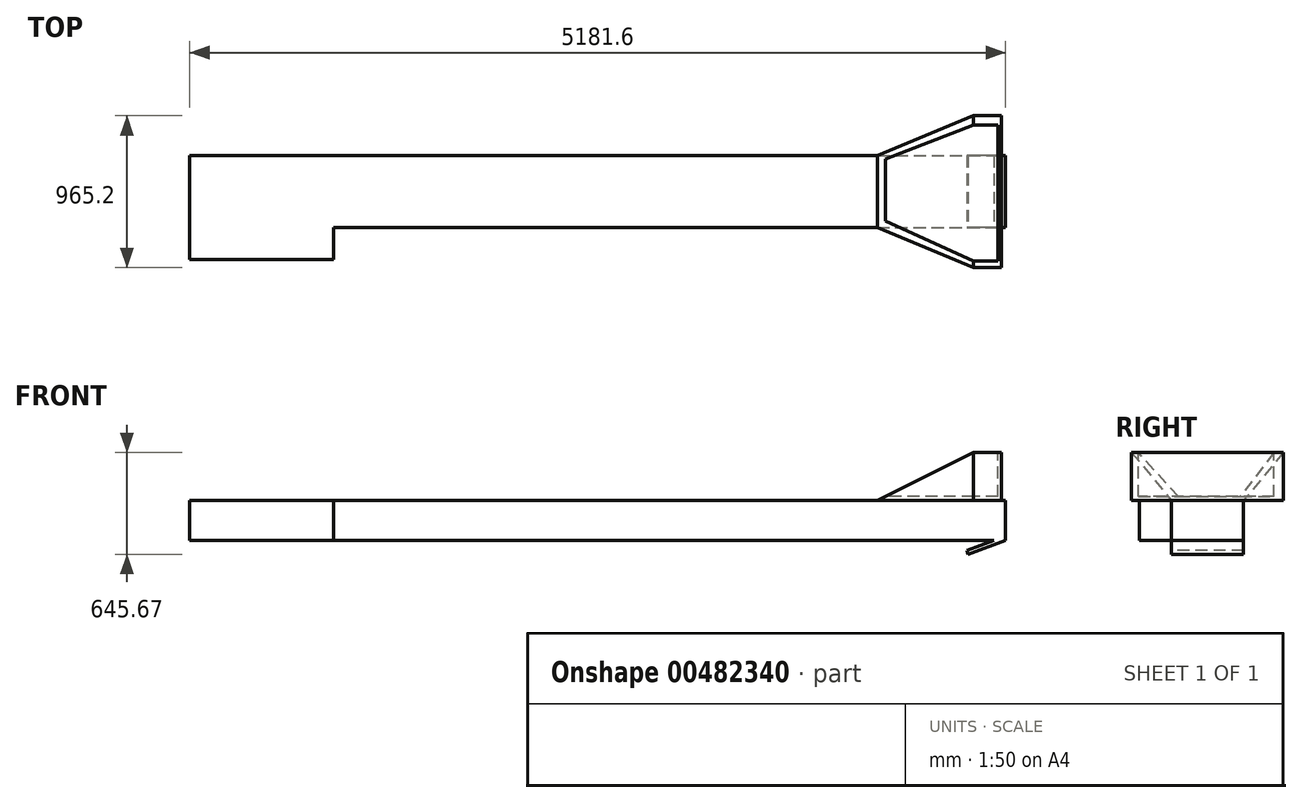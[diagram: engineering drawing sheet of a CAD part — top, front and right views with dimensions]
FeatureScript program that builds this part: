
annotation { "Feature Type Name" : "Feature", "Feature Type Description" : "" }
export const myFeature = defineFeature(function(context is Context, id is Id, definition is map)
    precondition{}
    {
        {
            var Q0;
            Q0=qCreatedBy(makeId("Top.planeOp"),FACE);
            var sketch = newSketch(context, id + "F0", { "sketchPlane" : qUnion([Q0])});
            skLineSegment(sketch, "E0.bottom", {"start": v(0, 0) * mm, "end": v(5181.6, 0) * mm});
            skLineSegment(sketch, "E0.top", {"start": v(0, 457.2) * mm, "end": v(5181.6, 457.2) * mm});
            skLineSegment(sketch, "E0.left", {"start": v(0, 0) * mm, "end": v(0, 457.2) * mm});
            skLineSegment(sketch, "E0.right", {"start": v(5181.6, 0) * mm, "end": v(5181.6, 457.2) * mm});
            skSolve(sketch);
        }
        {
            var Q0;
            Q0 = qSketchRegion(id + "F0", true);
            extrude(context, id + "F1", {"entities" : qUnion([Q0]), "depth" : 254 * mm, "offsetDistance" : 25.4 * mm});
        }
        {
            var Q0;
            Q0=makeQuery(id+"F1.opExtrude","SWEPT_FACE",FACE,{"disambiguationData":[OSD([sQuery(id+"F0.wireOp",EDGE,"E0.bottom")])]});
            var sketch = newSketch(context, id + "F2", { "sketchPlane" : qUnion([Q0])});
            skLineSegment(sketch, "E1.bottom", {"start": v(0, 0) * mm, "end": v(914.4, 0) * mm});
            skLineSegment(sketch, "E1.top", {"start": v(0, 254) * mm, "end": v(914.4, 254) * mm});
            skLineSegment(sketch, "E1.left", {"start": v(0, 0) * mm, "end": v(0, 254) * mm});
            skLineSegment(sketch, "E1.right", {"start": v(914.4, 0) * mm, "end": v(914.4, 254) * mm});
            skSolve(sketch);
        }
        {
            var Q0;
            Q0 = qSketchRegion(id + "F2", true);
            extrude(context, id + "F3", {"entities" : qUnion([Q0]), "operationType" : NewBodyOperationType.ADD, "depth" : 203.2 * mm, "offsetDistance" : 25.4 * mm});
        }
        {
            var Q0;
            Q0=makeQuery(id+"F1.opExtrude","SWEPT_FACE",FACE,{"disambiguationData":[OSD([sQuery(id+"F0.wireOp",EDGE,"E0.bottom")])]});
            cPlane(context, id + "F4", {"entities" : qUnion([Q0]), "cplaneType" : CPlaneType.OFFSET, "offset" : 254 * mm, "width" : 152.4 * mm, "height" : 152.4 * mm});
        }
        {
            var Q0;
            Q0=qCreatedBy(id+"F4.planeOp",FACE);
            var sketch = newSketch(context, id + "F5", { "sketchPlane" : qUnion([Q0])});
            skLineSegment(sketch, "E2", {"start": v(5156.2, 254) * mm, "end": v(5156.2, 558.8) * mm});
            skLineSegment(sketch, "E3", {"start": v(5156.2, 558.8) * mm, "end": v(4978.4, 558.8) * mm});
            skLineSegment(sketch, "E4", {"start": v(4978.4, 558.8) * mm, "end": v(4368.8, 254) * mm});
            skLineSegment(sketch, "E5", {"start": v(4368.8, 254) * mm, "end": v(5156.2, 254) * mm});
            skSolve(sketch);
        }
        {
            var Q0;
            Q0 = qSketchRegion(id + "F5", true);
            extrude(context, id + "F6", {"entities" : qUnion([Q0]), "operationType" : NewBodyOperationType.ADD, "oppositeDirection" : true, "depth" : 965.2 * mm, "offsetDistance" : 25.4 * mm});
        }
        {
            var Q0;
            Q0=makeQuery(id+"F6.opExtrude","SWEPT_FACE",FACE,{"disambiguationData":[OSD([sQuery(id+"F5.wireOp",EDGE,"E3")])]});
            var sketch = newSketch(context, id + "F7", { "sketchPlane" : qUnion([Q0])});
            skLineSegment(sketch, "E6", {"start": v(4368.8, 711.2) * mm, "end": v(4978.4, 711.2) * mm});
            skLineSegment(sketch, "E7", {"start": v(4978.4, 711.2) * mm, "end": v(4368.8, 457.2) * mm});
            skLineSegment(sketch, "E8", {"start": v(4368.8, 457.2) * mm, "end": v(4368.8, 711.2) * mm});
            skLineSegment(sketch, "E9", {"start": v(4978.4, -254) * mm, "end": v(4368.8, 0) * mm});
            skLineSegment(sketch, "E10", {"start": v(4368.8, 0) * mm, "end": v(4368.8, -254) * mm});
            skLineSegment(sketch, "E11", {"start": v(4368.8, -254) * mm, "end": v(4978.4, -254) * mm});
            skSolve(sketch);
        }
        {
            var Q0;
            Q0 = qSketchRegion(id + "F7", true);
            extrude(context, id + "F8", {"entities" : qUnion([Q0]), "operationType" : NewBodyOperationType.REMOVE, "endBound" : BoundingType.THROUGH_ALL, "oppositeDirection" : true, "depth" : 25.4 * mm, "offsetDistance" : 25.4 * mm});
        }
        {
            var Q0;
            Q0=makeQuery(id+"F6.opExtrude","SWEPT_FACE",FACE,{"disambiguationData":[OSD([sQuery(id+"F5.wireOp",EDGE,"E3")])]});
            var sketch = newSketch(context, id + "F9", { "sketchPlane" : qUnion([Q0])});
            skLineSegment(sketch, "E12", {"start": v(5132.56, 650.2) * mm, "end": v(4978.4, 650.2) * mm});
            skLineSegment(sketch, "E13", {"start": v(4978.4, 650.2) * mm, "end": v(4409.44, 430.9) * mm});
            skLineSegment(sketch, "E14", {"start": v(4409.44, 430.9) * mm, "end": v(4409.44, 47.15) * mm});
            skLineSegment(sketch, "E15", {"start": v(4409.44, 47.15) * mm, "end": v(4978.4, -211.3) * mm});
            skLineSegment(sketch, "E16", {"start": v(4978.4, -211.3) * mm, "end": v(5132.56, -211.3) * mm});
            skLineSegment(sketch, "E17", {"start": v(5132.56, -211.3) * mm, "end": v(5132.56, 650.2) * mm});
            skSolve(sketch);
        }
        {
            var Q0;
            {var subQ0=sQuery(id+"F9.wireOp",EDGE,"E13");Q0=makeQuery(id+"F9.imprint","IMPRINT",FACE,{"disambiguationData":[TD([[makeQuery(id+"F9.imprint","IMPRINT",EDGE,{"derivedFrom":subQ0}),1.0]])]});}
            var Q1;
            {var subQ0=sQuery(id+"F9.wireOp",EDGE,"E12");Q1=makeQuery(id+"F9.imprint","IMPRINT",FACE,{"disambiguationData":[TD([[makeQuery(id+"F9.imprint","IMPRINT",EDGE,{"derivedFrom":subQ0}),1.0]])]});}
            var Q2;
            {var subQ0=sQuery(id+"F0.wireOp",EDGE,"E0.left");var subQ1=sQuery(id+"F0.wireOp",EDGE,"E0.top");var subQ4=sQuery(id+"F2.wireOp",EDGE,"E1.top");var subQ5=sQuery(id+"F0.wireOp",EDGE,"E0.bottom");Q2=makeQuery(id+"F6.boolean.opBoolean","SPLIT",FACE,{"disambiguationData":[TD([makeQuery(id+"F1.opExtrude","SWEPT_FACE",FACE,{"disambiguationData":[OSD([subQ0])]})])],"derivedFrom":makeQuery(id+"F3.boolean.opBoolean","MERGE",FACE,{"derivedFrom":[makeQuery(id+"F1.opExtrude","CAP_FACE",FACE,{"disambiguationData":[OSD([subQ5,subQ1,subQ0,sQuery(id+"F0.wireOp",EDGE,"E0.right")])],"isStart":false}),makeQuery(id+"F3.opExtrude","SWEPT_FACE",FACE,{"disambiguationData":[OSD([subQ4])]})]})});}
            extrude(context, id + "F10", {"entities" : qUnion([Q0, Q1]), "operationType" : NewBodyOperationType.REMOVE, "endBound" : BoundingType.UP_TO_SURFACE, "oppositeDirection" : true, "depth" : 25.4 * mm, "endBoundEntityFace" : qUnion([Q2]), "hasOffset" : true, "offsetDistance" : 25.4 * mm});
        }
        {
            var Q0;
            Q0=makeQuery(id+"F1.opExtrude","CAP_EDGE",EDGE,{"disambiguationData":[OSD([sQuery(id+"F0.wireOp",EDGE,"E0.right")])],"isStart":true});
            var Q1;
            Q1=makeQuery(id+"F3.boolean.opBoolean","MERGE",FACE,{"derivedFrom":[makeQuery(id+"F1.opExtrude","CAP_FACE",FACE,{"disambiguationData":[OSD([sQuery(id+"F0.wireOp",EDGE,"E0.bottom"),sQuery(id+"F0.wireOp",EDGE,"E0.top"),sQuery(id+"F0.wireOp",EDGE,"E0.left"),sQuery(id+"F0.wireOp",EDGE,"E0.right")])],"isStart":true}),makeQuery(id+"F3.opExtrude","SWEPT_FACE",FACE,{"disambiguationData":[OSD([sQuery(id+"F2.wireOp",EDGE,"E1.bottom")])]})]});
            cPlane(context, id + "F11", {"entities" : qUnion([Q0, Q1]), "cplaneType" : CPlaneType.LINE_ANGLE, "offset" : 25.4 * mm, "angle" : 20 * degree, "oppositeDirection" : true, "width" : 152.4 * mm, "height" : 152.4 * mm});
        }
        {
            var Q0;
            Q0=qCreatedBy(id+"F11.planeOp",FACE);
            var sketch = newSketch(context, id + "F12", { "sketchPlane" : qUnion([Q0])});
            skLineSegment(sketch, "E18.bottom", {"start": v(4869.11, 457.2) * mm, "end": v(4615.11, 457.2) * mm});
            skLineSegment(sketch, "E18.top", {"start": v(4869.11, 0) * mm, "end": v(4615.11, 0) * mm});
            skLineSegment(sketch, "E18.left", {"start": v(4869.11, 457.2) * mm, "end": v(4869.11, 0) * mm});
            skLineSegment(sketch, "E18.right", {"start": v(4615.11, 457.2) * mm, "end": v(4615.11, 0) * mm});
            skSolve(sketch);
        }
        {
            var Q0;
            Q0 = qSketchRegion(id + "F12", true);
            extrude(context, id + "F13", {"entities" : qUnion([Q0]), "operationType" : NewBodyOperationType.ADD, "depth" : 25.4 * mm, "offsetDistance" : 25.4 * mm});
        }
    });
